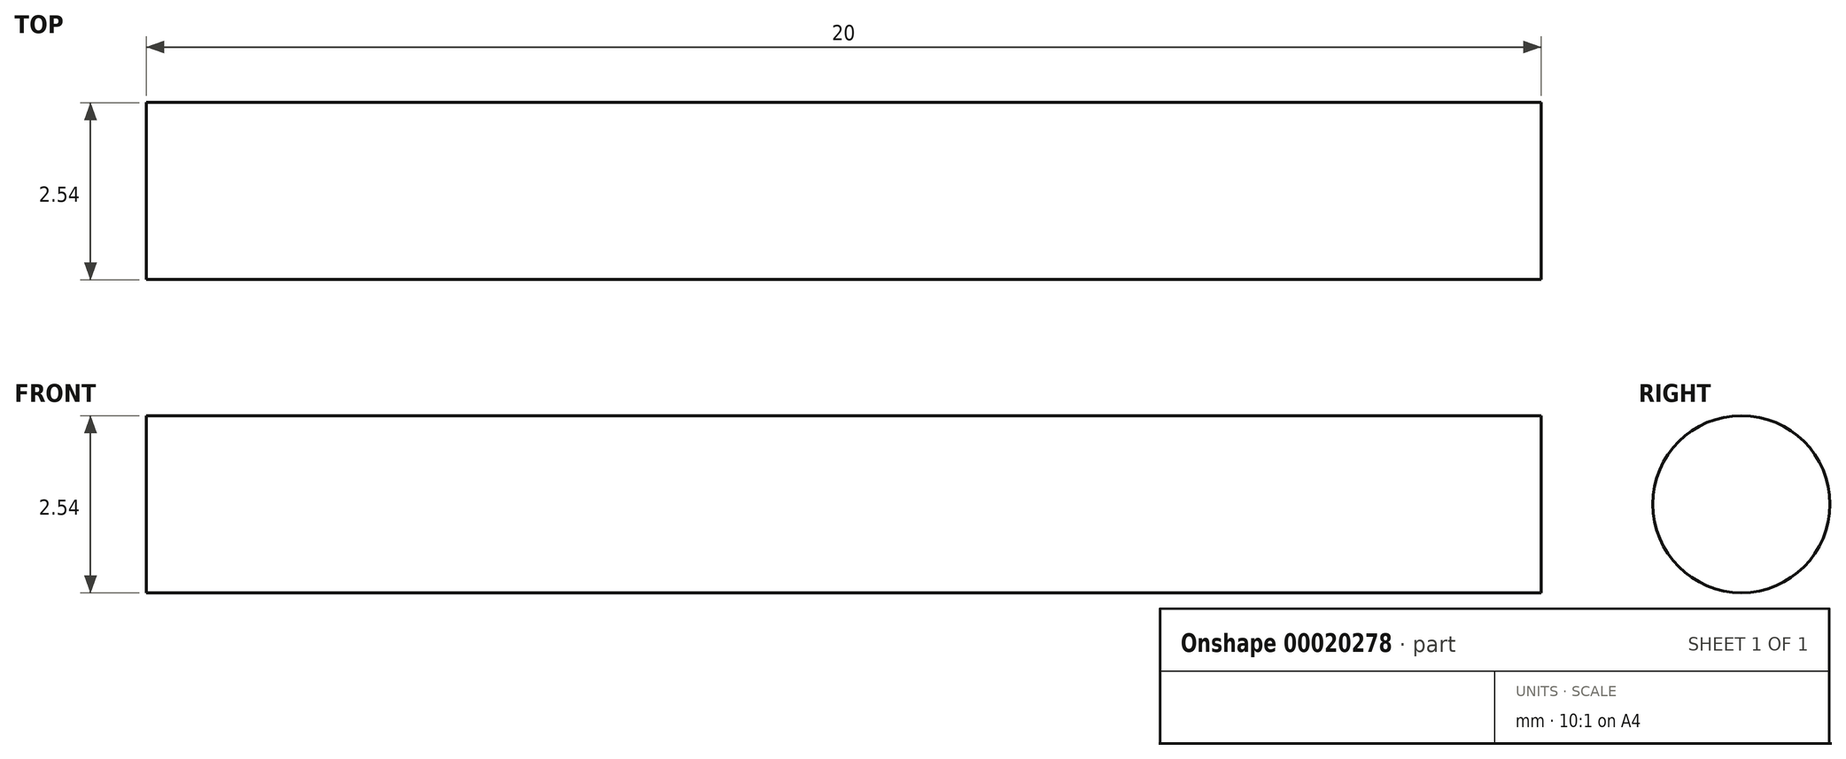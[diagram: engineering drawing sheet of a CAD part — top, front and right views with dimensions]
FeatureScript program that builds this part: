
annotation { "Feature Type Name" : "Feature", "Feature Type Description" : "" }
export const myFeature = defineFeature(function(context is Context, id is Id, definition is map)
    precondition{}
    {
        {
            var Q0;
            Q0=qCreatedBy(makeId("Right.planeOp"),FACE);
            var sketch = newSketch(context, id + "F0", { "sketchPlane" : qUnion([Q0])});
            skCircle(sketch, "E0", {"center": v(-38.4, 51.46) * mm, "radius": 1.27 * mm});
            skSolve(sketch);
        }
        {
            var Q0;
            Q0=makeQuery(id+"F0.imprint","IMPRINT",FACE,{"disambiguationData":[TD([[makeQuery(id+"F0.imprint","IMPRINT",EDGE,{"derivedFrom":sQuery(id+"F0.wireOp",EDGE,"E0")}),1.0]])]});
            extrude(context, id + "F1", {"entities" : qUnion([Q0]), "depth" : 20 * mm});
        }
    });
